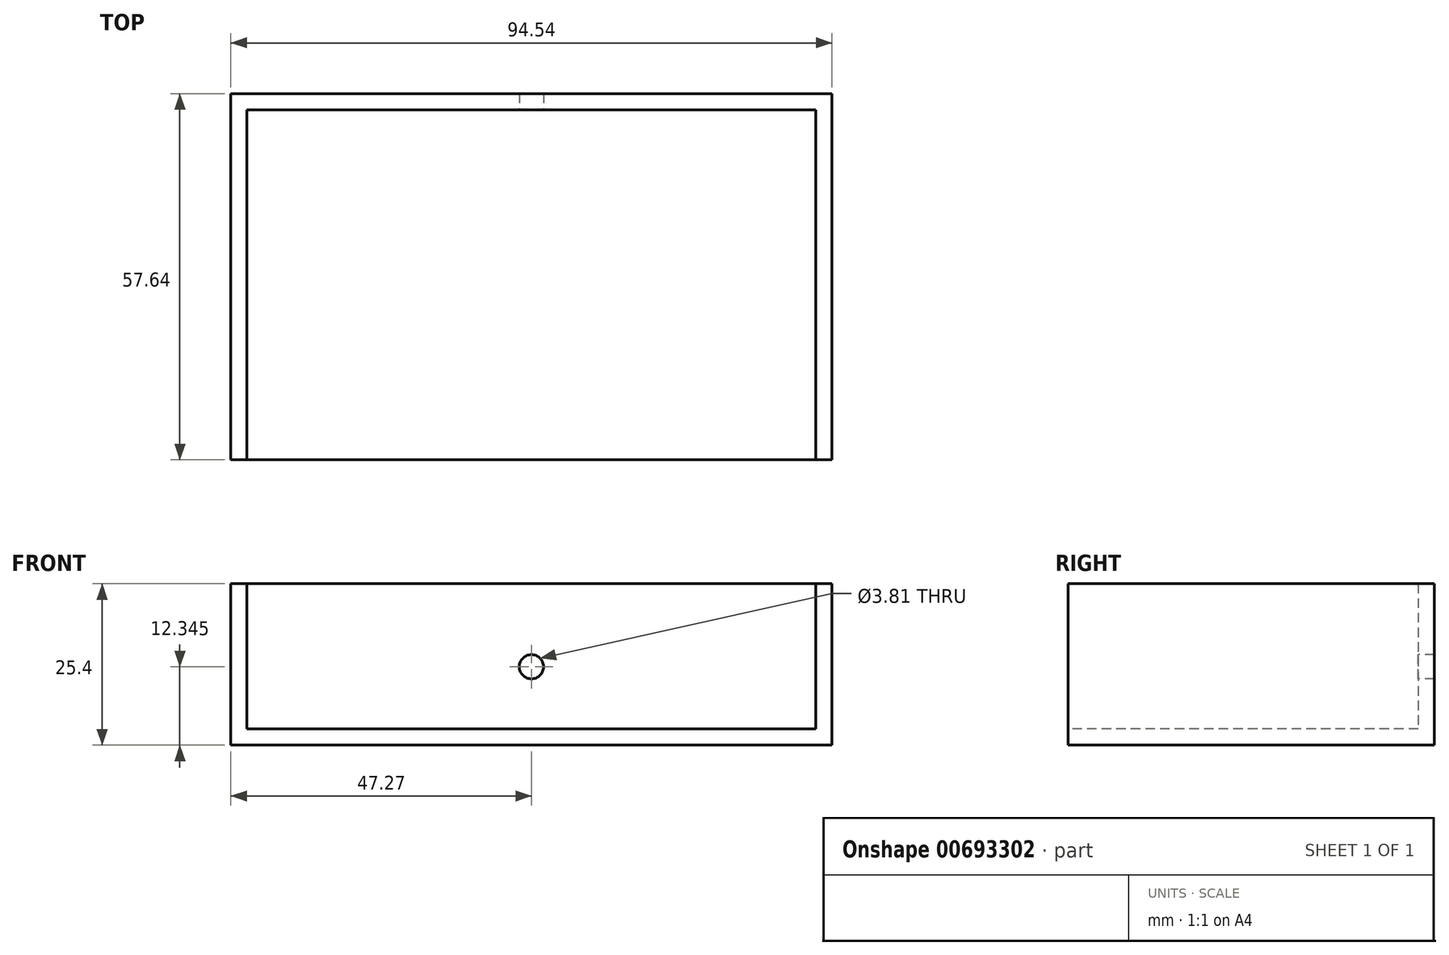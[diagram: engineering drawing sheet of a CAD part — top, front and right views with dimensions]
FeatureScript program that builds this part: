
annotation { "Feature Type Name" : "Feature", "Feature Type Description" : "" }
export const myFeature = defineFeature(function(context is Context, id is Id, definition is map)
    precondition{}
    {
        {
            var Q0;
            Q0=qCreatedBy(makeId("Top.planeOp"),FACE);
            var sketch = newSketch(context, id + "F0", { "sketchPlane" : qUnion([Q0])});
            skLineSegment(sketch, "E0.bottom", {"start": v(-47.27, 28.82) * mm, "end": v(47.27, 28.82) * mm});
            skLineSegment(sketch, "E0.top", {"start": v(-47.27, -28.82) * mm, "end": v(47.27, -28.82) * mm});
            skLineSegment(sketch, "E0.left", {"start": v(-47.27, 28.82) * mm, "end": v(-47.27, -28.82) * mm});
            skLineSegment(sketch, "E0.right", {"start": v(47.27, 28.82) * mm, "end": v(47.27, -28.82) * mm});
            skPoint(sketch, "E0.middle", {"position": v(0, 0) * mm});
            skSolve(sketch);
        }
        {
            var Q0;
            Q0 = qSketchRegion(id + "F0", true);
            extrude(context, id + "F1", {"entities" : qUnion([Q0]), "depth" : 25.4 * mm, "offsetDistance" : 25.4 * mm});
        }
        {
            var Q0;
            Q0=makeQuery(id+"F1.opExtrude","CAP_FACE",FACE,{"disambiguationData":[OSD([sQuery(id+"F0.wireOp",EDGE,"E0.bottom"),sQuery(id+"F0.wireOp",EDGE,"E0.top"),sQuery(id+"F0.wireOp",EDGE,"E0.left"),sQuery(id+"F0.wireOp",EDGE,"E0.right")])],"isStart":false});
            var Q1;
            Q1=makeQuery(id+"F1.opExtrude","SWEPT_FACE",FACE,{"disambiguationData":[OSD([sQuery(id+"F0.wireOp",EDGE,"E0.top")])]});
            shell(context, id + "F2", {"entities" : qUnion([Q0, Q1]), "thickness" : 2.54 * mm});
        }
        {
            var Q0;
            Q0=makeQuery(id+"F2.opShell","OFFSET_FACE",FACE,{"disambiguationData":[OSD([sQuery(id+"F0.wireOp",EDGE,"E0.bottom")])]});
            var sketch = newSketch(context, id + "F3", { "sketchPlane" : qUnion([Q0])});
            skPoint(sketch, "E1", {"position": v(0, 12.35) * mm});
            skPoint(sketch, "E1.positionSnap0", {"position": v(0, 2.54) * mm});
            skSolve(sketch);
        }
        {
            var Q0;
            Q0=sQuery(id+"F3.wireOp",VERTEX,"E1");
            var Q1;
            Q1=makeQuery(id+"F1.opExtrude","SWEPT_BODY",BODY,{"disambiguationData":[OSD([sQuery(id+"F0.wireOp",EDGE,"E0.bottom"),sQuery(id+"F0.wireOp",EDGE,"E0.top"),sQuery(id+"F0.wireOp",EDGE,"E0.left"),sQuery(id+"F0.wireOp",EDGE,"E0.right")])]});
            hole(context, id + "F4", {"style" : HoleStyle.SIMPLE, "endStyle" : HoleEndStyle.THROUGH, "holeDiameter" : 3.8 * mm, "majorDiameter" : 6.35 * mm, "isTappedThrough" : true, "tappedDepth" : 12.7 * mm, "tapClearance" : 3, "locations" : qUnion([Q0]), "scope" : qUnion([Q1])});
        }
    });
